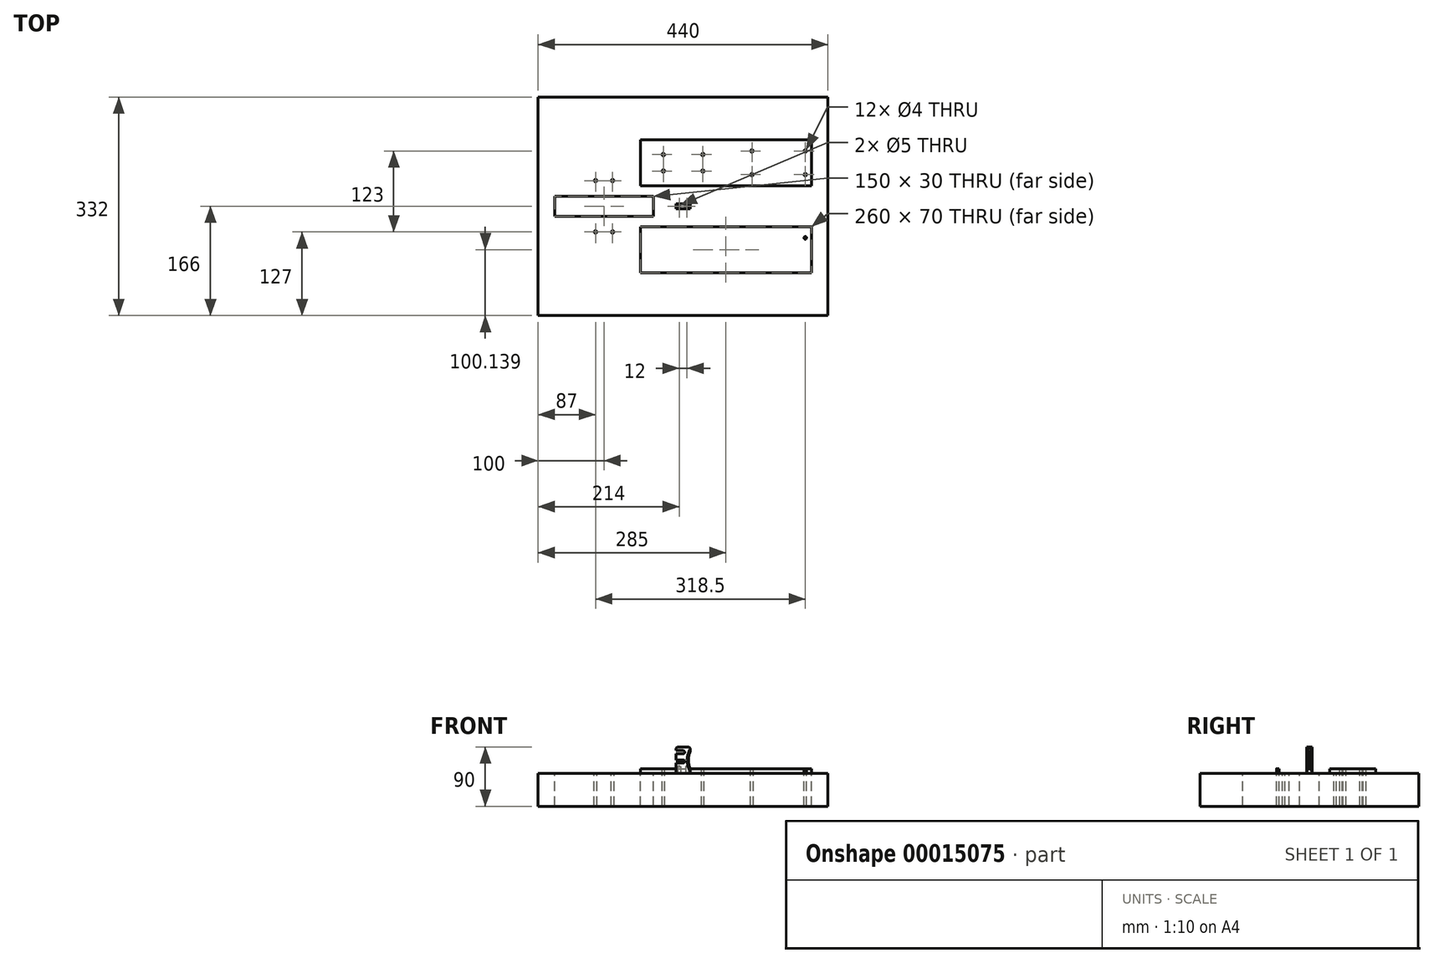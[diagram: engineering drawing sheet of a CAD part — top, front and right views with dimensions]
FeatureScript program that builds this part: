
annotation { "Feature Type Name" : "Feature", "Feature Type Description" : "" }
export const myFeature = defineFeature(function(context is Context, id is Id, definition is map)
    precondition{}
    {
        {
            var Q0;
            Q0=qCreatedBy(makeId("Top.planeOp"),FACE);
            var sketch = newSketch(context, id + "F0", { "sketchPlane" : qUnion([Q0])});
            skLineSegment(sketch, "E0.rect.bottom", {"start": v(145, -66) * mm, "end": v(-120, -66) * mm, "construction": true});
            skLineSegment(sketch, "E0.rect.top", {"start": v(145, 66) * mm, "end": v(-120, 66) * mm, "construction": true});
            skLineSegment(sketch, "E0.rect.left", {"start": v(145, -66) * mm, "end": v(145, 66) * mm, "construction": true});
            skLineSegment(sketch, "E0.rect.right", {"start": v(-120, -66) * mm, "end": v(-120, 66) * mm, "construction": true});
            skPoint(sketch, "E0.rect.middle", {"position": v(0, 0) * mm});
            skLineSegment(sketch, "E1.0", {"start": v(220, 166) * mm, "end": v(-220, 166) * mm});
            skLineSegment(sketch, "E1.1", {"start": v(220, -166) * mm, "end": v(220, 166) * mm});
            skLineSegment(sketch, "E1.2", {"start": v(220, -166) * mm, "end": v(-220, -166) * mm});
            skLineSegment(sketch, "E1.3", {"start": v(-220, -166) * mm, "end": v(-220, 166) * mm});
            skLineSegment(sketch, "E2", {"start": v(-220, 0) * mm, "end": v(220, 0) * mm, "construction": true});
            skLineSegment(sketch, "E3.rect.bottom", {"start": v(185.5, 48) * mm, "end": v(104.5, 48) * mm, "construction": true});
            skLineSegment(sketch, "E3.rect.top", {"start": v(185.5, 84) * mm, "end": v(104.5, 84) * mm, "construction": true});
            skLineSegment(sketch, "E3.rect.left", {"start": v(185.5, 48) * mm, "end": v(185.5, 84) * mm, "construction": true});
            skLineSegment(sketch, "E3.rect.right", {"start": v(104.5, 48) * mm, "end": v(104.5, 84) * mm, "construction": true});
            skPoint(sketch, "E3.rect.middle", {"position": v(145, 66) * mm});
            skCircle(sketch, "E4", {"center": v(104.5, 84) * mm, "radius": 2 * mm});
            skCircle(sketch, "E5", {"center": v(185.5, 84) * mm, "radius": 2 * mm});
            skCircle(sketch, "E6", {"center": v(185.5, 48) * mm, "radius": 2 * mm});
            skCircle(sketch, "E7", {"center": v(104.5, 48) * mm, "radius": 2 * mm});
            skLineSegment(sketch, "E8.0.MirrorCS", {"start": v(185.5, -48) * mm, "end": v(104.5, -48) * mm, "construction": true});
            skLineSegment(sketch, "E9.0.MirrorCS", {"start": v(104.5, -48) * mm, "end": v(104.5, -84) * mm, "construction": true});
            skLineSegment(sketch, "E10.0.MirrorCS", {"start": v(185.5, -84) * mm, "end": v(104.5, -84) * mm, "construction": true});
            skLineSegment(sketch, "E11.0.MirrorCS", {"start": v(185.5, -48) * mm, "end": v(185.5, -84) * mm, "construction": true});
            skCircle(sketch, "E12.0.MirrorC", {"center": v(185.5, -48) * mm, "radius": 2 * mm});
            skCircle(sketch, "E13.0.MirrorC", {"center": v(104.5, -48) * mm, "radius": 2 * mm});
            skCircle(sketch, "E14.0.MirrorC", {"center": v(104.5, -84) * mm, "radius": 2 * mm});
            skCircle(sketch, "E15.0.MirrorC", {"center": v(185.5, -84) * mm, "radius": 2 * mm});
            skLineSegment(sketch, "E16.rect.bottom", {"start": v(-107, -39) * mm, "end": v(-133, -39) * mm, "construction": true});
            skLineSegment(sketch, "E16.rect.top", {"start": v(-107, 39) * mm, "end": v(-133, 39) * mm, "construction": true});
            skLineSegment(sketch, "E16.rect.left", {"start": v(-107, -39) * mm, "end": v(-107, 39) * mm, "construction": true});
            skLineSegment(sketch, "E16.rect.right", {"start": v(-133, -39) * mm, "end": v(-133, 39) * mm, "construction": true});
            skPoint(sketch, "E16.rect.middle", {"position": v(-120, 0) * mm});
            skCircle(sketch, "E17", {"center": v(-133, 39) * mm, "radius": 2 * mm});
            skCircle(sketch, "E18", {"center": v(-107, 39) * mm, "radius": 2 * mm});
            skCircle(sketch, "E19", {"center": v(-107, -39) * mm, "radius": 2 * mm});
            skCircle(sketch, "E20", {"center": v(-133, -39) * mm, "radius": 2 * mm});
            skLineSegment(sketch, "E21", {"start": v(0, 166) * mm, "end": v(0, -166) * mm, "construction": true});
            skLineSegment(sketch, "E22.rect.bottom", {"start": v(30, 53.5) * mm, "end": v(-30, 53.5) * mm, "construction": true});
            skLineSegment(sketch, "E22.rect.top", {"start": v(30, 78.5) * mm, "end": v(-30, 78.5) * mm, "construction": true});
            skLineSegment(sketch, "E22.rect.left", {"start": v(30, 53.5) * mm, "end": v(30, 78.5) * mm, "construction": true});
            skLineSegment(sketch, "E22.rect.right", {"start": v(-30, 53.5) * mm, "end": v(-30, 78.5) * mm, "construction": true});
            skPoint(sketch, "E22.rect.middle", {"position": v(0, 66) * mm});
            skCircle(sketch, "E23", {"center": v(-30, 78.5) * mm, "radius": 2 * mm});
            skCircle(sketch, "E24", {"center": v(-30, 53.5) * mm, "radius": 2 * mm});
            skCircle(sketch, "E25", {"center": v(30, 53.5) * mm, "radius": 2 * mm});
            skCircle(sketch, "E26", {"center": v(30, 78.5) * mm, "radius": 2 * mm});
            skLineSegment(sketch, "E27.0.MirrorCS", {"start": v(30, -53.5) * mm, "end": v(-30, -53.5) * mm, "construction": true});
            skLineSegment(sketch, "E28.0.MirrorCS", {"start": v(-30, -53.5) * mm, "end": v(-30, -78.5) * mm, "construction": true});
            skLineSegment(sketch, "E29.0.MirrorCS", {"start": v(30, -78.5) * mm, "end": v(-30, -78.5) * mm, "construction": true});
            skLineSegment(sketch, "E30.0.MirrorCS", {"start": v(30, -53.5) * mm, "end": v(30, -78.5) * mm, "construction": true});
            skCircle(sketch, "E31.0.MirrorC", {"center": v(30, -53.5) * mm, "radius": 2 * mm});
            skCircle(sketch, "E32.0.MirrorC", {"center": v(30, -78.5) * mm, "radius": 2 * mm});
            skCircle(sketch, "E33.0.MirrorC", {"center": v(-30, -78.5) * mm, "radius": 2 * mm});
            skCircle(sketch, "E34.0.MirrorC", {"center": v(-30, -53.5) * mm, "radius": 2 * mm});
            skLineSegment(sketch, "E35.rect.bottom", {"start": v(-45, -15) * mm, "end": v(-195, -15) * mm});
            skLineSegment(sketch, "E35.rect.top", {"start": v(-45, 15) * mm, "end": v(-195, 15) * mm});
            skLineSegment(sketch, "E35.rect.left", {"start": v(-45, -15) * mm, "end": v(-45, 15) * mm});
            skLineSegment(sketch, "E35.rect.right", {"start": v(-195, -15) * mm, "end": v(-195, 15) * mm});
            skLineSegment(sketch, "E36.bottom", {"start": v(-65, 100.86) * mm, "end": v(195, 100.86) * mm});
            skLineSegment(sketch, "E36.top", {"start": v(-65, 30.86) * mm, "end": v(195, 30.86) * mm});
            skLineSegment(sketch, "E36.left", {"start": v(-65, 100.86) * mm, "end": v(-65, 30.86) * mm});
            skLineSegment(sketch, "E36.right", {"start": v(195, 100.86) * mm, "end": v(195, 30.86) * mm});
            skLineSegment(sketch, "E37.0.MirrorCS", {"start": v(-65, -30.86) * mm, "end": v(195, -30.86) * mm});
            skLineSegment(sketch, "E38.0.MirrorCS", {"start": v(-65, -100.86) * mm, "end": v(195, -100.86) * mm});
            skLineSegment(sketch, "E39.0.MirrorCS", {"start": v(-65, -100.86) * mm, "end": v(-65, -30.86) * mm});
            skLineSegment(sketch, "E40.0.MirrorCS", {"start": v(195, -100.86) * mm, "end": v(195, -30.86) * mm});
            skSolve(sketch);
        }
        {
            var Q0;
            Q0=makeQuery(id+"F0.imprint","IMPRINT",FACE,{"disambiguationData":[TD([[makeQuery(id+"F0.imprint","IMPRINT",EDGE,{"derivedFrom":sQuery(id+"F0.wireOp",EDGE,"E1.0")}),1.0]])]});
            var Q1;
            Q1=makeQuery(id+"F0.imprint","IMPRINT",FACE,{"disambiguationData":[TD([[makeQuery(id+"F0.imprint","IMPRINT",EDGE,{"derivedFrom":sQuery(id+"F0.wireOp",EDGE,"E4")}),-1.0]])]});
            var Q2;
            Q2=makeQuery(id+"F0.imprint","IMPRINT",FACE,{"disambiguationData":[TD([[makeQuery(id+"F0.imprint","IMPRINT",EDGE,{"derivedFrom":sQuery(id+"F0.wireOp",EDGE,"E12.0.MirrorC")}),1.0]])]});
            extrude(context, id + "F1", {"entities" : qUnion([Q0, Q1, Q2]), "oppositeDirection" : true, "depth" : 50 * mm});
        }
        {
            var Q0;
            Q0=makeQuery(id+"F0.imprint","IMPRINT",FACE,{"disambiguationData":[TD([[makeQuery(id+"F0.imprint","IMPRINT",EDGE,{"derivedFrom":sQuery(id+"F0.wireOp",EDGE,"E4")}),-1.0]])]});
            var Q1;
            Q1=makeQuery(id+"F0.imprint","IMPRINT",FACE,{"disambiguationData":[TD([[makeQuery(id+"F0.imprint","IMPRINT",EDGE,{"derivedFrom":sQuery(id+"F0.wireOp",EDGE,"E12.0.MirrorC")}),1.0]])]});
            extrude(context, id + "F2", {"entities" : qUnion([Q0, Q1]), "operationType" : NewBodyOperationType.ADD, "depth" : 7 * mm});
        }
        {
            var Q0;
            Q0=qCreatedBy(makeId("Front.planeOp"),FACE);
            var sketch = newSketch(context, id + "F3", { "sketchPlane" : qUnion([Q0])});
            skLineSegment(sketch, "E41", {"start": v(0, 0) * mm, "end": v(0, 44.2) * mm, "construction": true});
            skLineSegment(sketch, "E42.rect.bottom", {"start": v(11, 0) * mm, "end": v(-11, 0) * mm});
            skLineSegment(sketch, "E42.rect.top", {"start": v(11, 40) * mm, "end": v(-11, 40) * mm});
            skLineSegment(sketch, "E42.rect.left", {"start": v(11, 0) * mm, "end": v(11, 7) * mm});
            skLineSegment(sketch, "E42.rect.right", {"start": v(-11, 0) * mm, "end": v(-11, 15.5) * mm});
            skPoint(sketch, "E42.rect.middle", {"position": v(0, 20) * mm});
            skLineSegment(sketch, "E43", {"start": v(11, 20) * mm, "end": v(-11, 20) * mm, "construction": true});
            skLineSegment(sketch, "E44", {"start": v(11, 18) * mm, "end": v(-11, 18) * mm, "construction": true});
            skLineSegment(sketch, "E45", {"start": v(11, 32) * mm, "end": v(-11, 32) * mm, "construction": true});
            skArc(sketch, "E46", {"start": v(0, 29.5) * mm, "mid": v(2.5, 32) * mm, "end": v(0, 34.5) * mm});
            skArc(sketch, "E47", {"start": v(0, 15.5) * mm, "mid": v(2.5, 18) * mm, "end": v(0, 20.5) * mm});
            skLineSegment(sketch, "E48", {"start": v(0, 34.5) * mm, "end": v(-11, 34.5) * mm});
            skLineSegment(sketch, "E49", {"start": v(0, 29.5) * mm, "end": v(-11, 29.5) * mm});
            skLineSegment(sketch, "E50", {"start": v(0, 20.5) * mm, "end": v(-11, 20.5) * mm});
            skLineSegment(sketch, "E51", {"start": v(0, 15.5) * mm, "end": v(-11, 15.5) * mm});
            skLineSegment(sketch, "E52.trimOffspring", {"start": v(-11, 20.5) * mm, "end": v(-11, 29.5) * mm});
            skLineSegment(sketch, "E53.trimOffspring", {"start": v(-11, 34.5) * mm, "end": v(-11, 40) * mm});
            skArc(sketch, "E54", {"start": v(11, 33) * mm, "mid": v(8.04, 20) * mm, "end": v(11, 7) * mm});
            skLineSegment(sketch, "E55.trimOffspring", {"start": v(11, 33) * mm, "end": v(11, 40) * mm});
            skSolve(sketch);
        }
        {
            var Q0;
            Q0=makeQuery(id+"F3.imprint","IMPRINT",FACE,{"disambiguationData":[TD([[makeQuery(id+"F3.imprint","IMPRINT",EDGE,{"derivedFrom":sQuery(id+"F3.wireOp",EDGE,"E42.rect.bottom")}),-1.0]])]});
            extrude(context, id + "F4", {"entities" : qUnion([Q0]), "endBound" : BoundingType.SYMMETRIC, "depth" : 8 * mm});
        }
        {
            var Q0;
            Q0=makeQuery(id+"F4.opExtrude","SWEPT_EDGE",EDGE,{"disambiguationData":[OSD([sQuery(id+"F3.wireOp",EDGE,"E42.rect.top"),sQuery(id+"F3.wireOp",EDGE,"E53.trimOffspring")])]});
            var Q1;
            Q1=makeQuery(id+"F4.opExtrude","SWEPT_EDGE",EDGE,{"disambiguationData":[OSD([sQuery(id+"F3.wireOp",EDGE,"E42.rect.top"),sQuery(id+"F3.wireOp",EDGE,"E55.trimOffspring")])]});
            var Q2;
            Q2=makeQuery(id+"F4.opExtrude","CAP_EDGE",EDGE,{"disambiguationData":[OSD([sQuery(id+"F3.wireOp",EDGE,"E54")])],"isStart":false});
            var Q3;
            Q3=makeQuery(id+"F4.opExtrude","CAP_EDGE",EDGE,{"disambiguationData":[OSD([sQuery(id+"F3.wireOp",EDGE,"E54")])],"isStart":true});
            chamfer(context, id + "F5", {"entities" : qUnion([Q0, Q1, Q2, Q3]), "width" : 2 * mm, "tangentPropagation" : true});
        }
        {
            var Q0;
            Q0=makeQuery(id+"F4.opExtrude","SWEPT_FACE",FACE,{"disambiguationData":[OSD([sQuery(id+"F3.wireOp",EDGE,"E42.rect.bottom")])]});
            var sketch = newSketch(context, id + "F6", { "sketchPlane" : qUnion([Q0])});
            skLineSegment(sketch, "E56", {"start": v(-11, 0) * mm, "end": v(11, 0) * mm, "construction": true});
            skPoint(sketch, "E57", {"position": v(-6, 0) * mm});
            skPoint(sketch, "E58", {"position": v(6, 0) * mm});
            skLineSegment(sketch, "E59", {"start": v(0, -4) * mm, "end": v(0, 4) * mm, "construction": true});
            skSolve(sketch);
        }
        {
            var Q0;
            Q0=sQuery(id+"F6.wireOp",VERTEX,"E57");
            var Q1;
            Q1=sQuery(id+"F6.wireOp",VERTEX,"E58");
            var Q2;
            Q2=makeQuery(id+"F4.opExtrude","SWEPT_BODY",BODY,{"disambiguationData":[OSD([sQuery(id+"F3.wireOp",EDGE,"E42.rect.bottom"),sQuery(id+"F3.wireOp",EDGE,"E42.rect.top"),sQuery(id+"F3.wireOp",EDGE,"E42.rect.left"),sQuery(id+"F3.wireOp",EDGE,"E42.rect.right"),sQuery(id+"F3.wireOp",EDGE,"E46"),sQuery(id+"F3.wireOp",EDGE,"E47"),sQuery(id+"F3.wireOp",EDGE,"E48"),sQuery(id+"F3.wireOp",EDGE,"E49"),sQuery(id+"F3.wireOp",EDGE,"E50"),sQuery(id+"F3.wireOp",EDGE,"E51"),sQuery(id+"F3.wireOp",EDGE,"E52.trimOffspring"),sQuery(id+"F3.wireOp",EDGE,"E53.trimOffspring"),sQuery(id+"F3.wireOp",EDGE,"E54"),sQuery(id+"F3.wireOp",EDGE,"E55.trimOffspring")])]});
            hole(context, id + "F7", {"style" : HoleStyle.SIMPLE, "holeDiameter" : 5 * mm, "endStyle" : HoleEndStyle.BLIND, "holeDepth" : 10 * mm, "locations" : qUnion([Q0, Q1]), "scope" : qUnion([Q2])});
        }
    });
